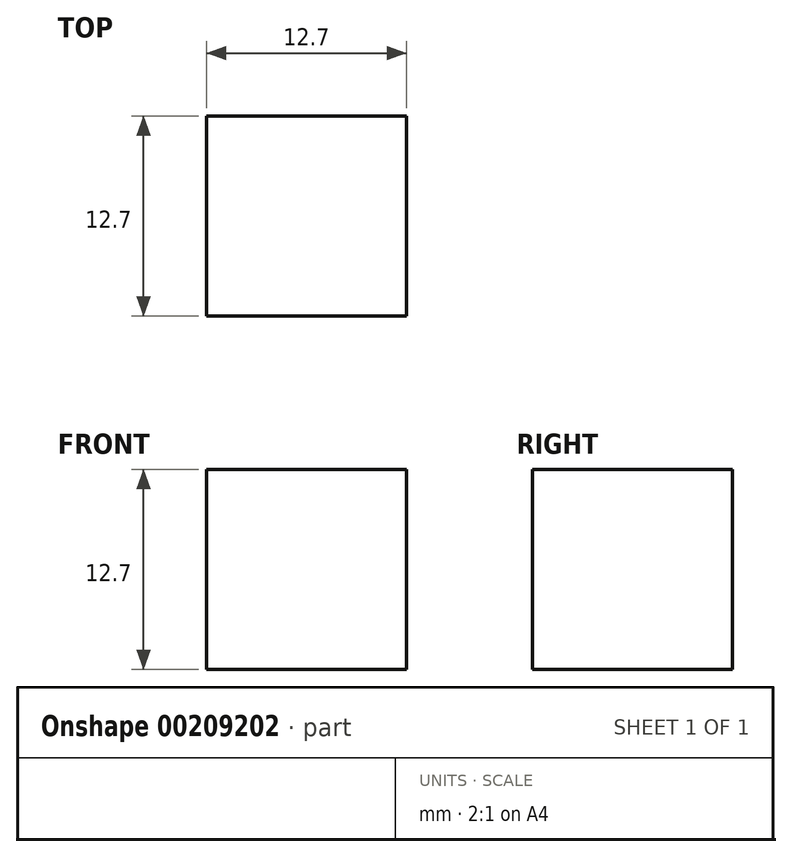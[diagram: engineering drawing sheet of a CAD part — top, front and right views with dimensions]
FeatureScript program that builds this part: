
annotation { "Feature Type Name" : "Feature", "Feature Type Description" : "" }
export const myFeature = defineFeature(function(context is Context, id is Id, definition is map)
    precondition{}
    {
        {
            var Q0;
            Q0=qCreatedBy(makeId("Front.planeOp"),FACE);
            var sketch = newSketch(context, id + "F0", { "sketchPlane" : qUnion([Q0])});
            skLineSegment(sketch, "E0.bottom", {"start": v(0, 0) * mm, "end": v(12.7, 0) * mm});
            skLineSegment(sketch, "E0.top", {"start": v(0, 12.7) * mm, "end": v(12.7, 12.7) * mm});
            skLineSegment(sketch, "E0.left", {"start": v(0, 0) * mm, "end": v(0, 12.7) * mm});
            skLineSegment(sketch, "E0.right", {"start": v(12.7, 0) * mm, "end": v(12.7, 12.7) * mm});
            skSolve(sketch);
        }
        {
            var Q0;
            Q0=makeQuery(id+"F0.imprint","IMPRINT",FACE,{"disambiguationData":[TD([[makeQuery(id+"F0.imprint","IMPRINT",EDGE,{"derivedFrom":sQuery(id+"F0.wireOp",EDGE,"E0.bottom")}),1.0]])]});
            extrude(context, id + "F1", {"entities" : qUnion([Q0]), "depth" : 12.7 * mm});
        }
    });
